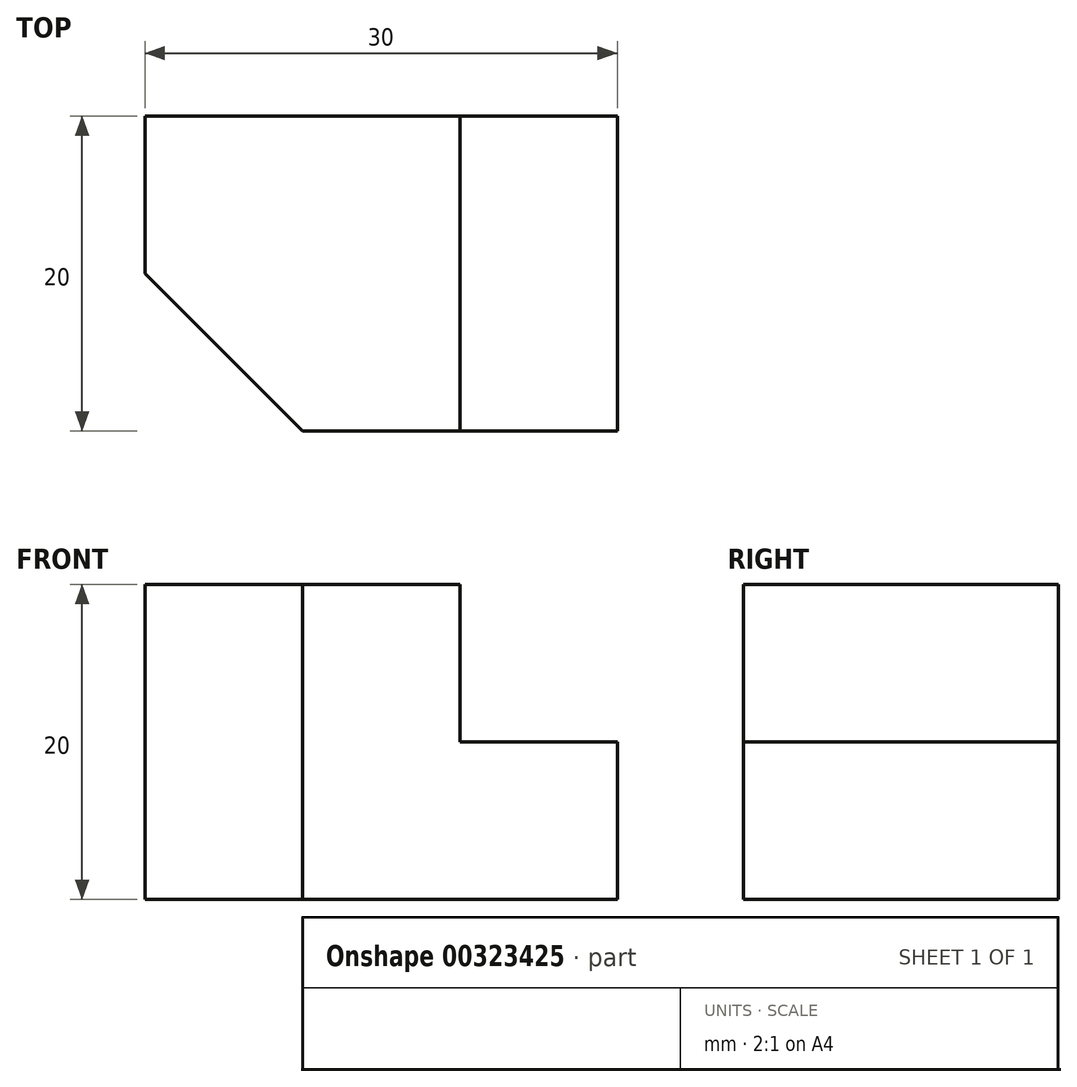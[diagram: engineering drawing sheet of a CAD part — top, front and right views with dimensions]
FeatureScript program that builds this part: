
annotation { "Feature Type Name" : "Feature", "Feature Type Description" : "" }
export const myFeature = defineFeature(function(context is Context, id is Id, definition is map)
    precondition{}
    {
        {
            var Q0;
            Q0=qCreatedBy(makeId("Front.planeOp"),FACE);
            var sketch = newSketch(context, id + "F0", { "sketchPlane" : qUnion([Q0])});
            skLineSegment(sketch, "E0.bottom", {"start": v(0, 0) * mm, "end": v(30, 0) * mm});
            skLineSegment(sketch, "E0.top", {"start": v(0, 20) * mm, "end": v(30, 20) * mm});
            skLineSegment(sketch, "E0.left", {"start": v(0, 0) * mm, "end": v(0, 20) * mm});
            skLineSegment(sketch, "E0.right", {"start": v(30, 0) * mm, "end": v(30, 20) * mm});
            skSolve(sketch);
        }
        {
            var Q0;
            Q0 = qSketchRegion(id + "F0", true);
            extrude(context, id + "F1", {"entities" : qUnion([Q0]), "depth" : 20 * mm});
        }
        {
            var Q0;
            Q0=makeQuery(id+"F1.opExtrude","SWEPT_FACE",FACE,{"disambiguationData":[OSD([sQuery(id+"F0.wireOp",EDGE,"E0.top")])]});
            var sketch = newSketch(context, id + "F2", { "sketchPlane" : qUnion([Q0])});
            skLineSegment(sketch, "E1", {"start": v(0, -10) * mm, "end": v(10, -20) * mm});
            skLineSegment(sketch, "E2", {"start": v(20, 0) * mm, "end": v(20, -20) * mm});
            skSolve(sketch);
        }
        {
            var Q0;
            {var subQ0=sQuery(id+"F2.wireOp",EDGE,"E1");Q0=makeQuery(id+"F2.imprint","IMPRINT",FACE,{"disambiguationData":[TD([[makeQuery(id+"F2.imprint","IMPRINT",EDGE,{"derivedFrom":subQ0}),-1.0]])]});}
            extrude(context, id + "F3", {"entities" : qUnion([Q0]), "operationType" : NewBodyOperationType.REMOVE, "oppositeDirection" : true, "depth" : 25 * mm});
        }
        {
            var Q0;
            {var subQ0=sQuery(id+"F2.wireOp",EDGE,"E2");Q0=makeQuery(id+"F2.imprint","IMPRINT",FACE,{"disambiguationData":[TD([[makeQuery(id+"F2.imprint","IMPRINT",EDGE,{"derivedFrom":subQ0}),1.0]])]});}
            extrude(context, id + "F4", {"entities" : qUnion([Q0]), "operationType" : NewBodyOperationType.REMOVE, "oppositeDirection" : true, "depth" : 10 * mm});
        }
    });
